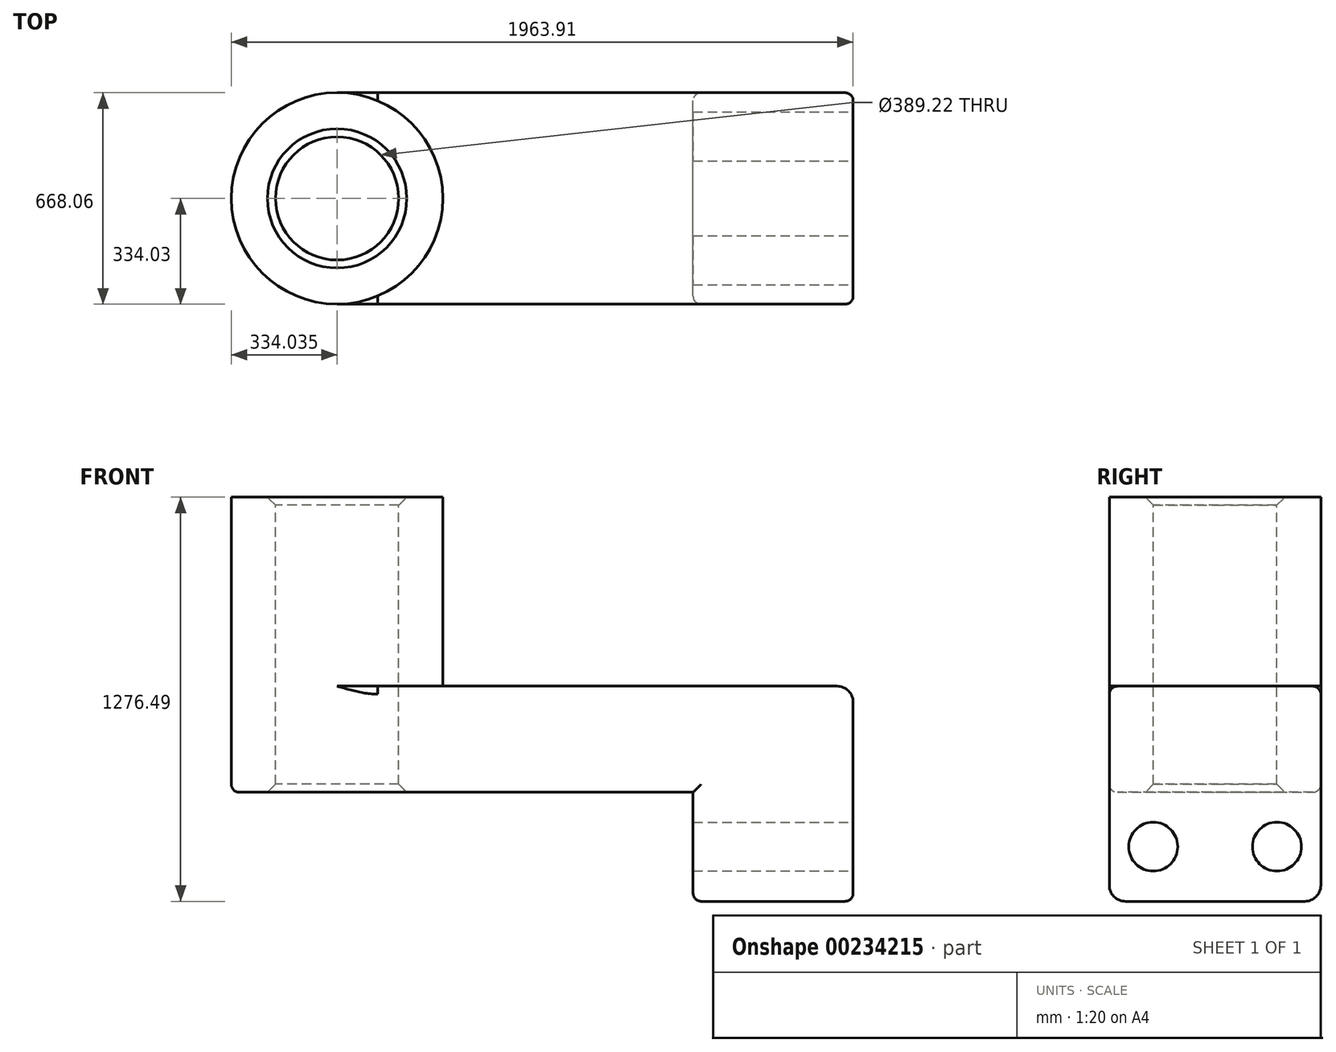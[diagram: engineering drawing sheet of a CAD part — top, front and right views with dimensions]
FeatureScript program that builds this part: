
annotation { "Feature Type Name" : "Feature", "Feature Type Description" : "" }
export const myFeature = defineFeature(function(context is Context, id is Id, definition is map)
    precondition{}
    {
        {
            var Q0;
            Q0=qCreatedBy(makeId("Top.planeOp"),FACE);
            var sketch = newSketch(context, id + "F0", { "sketchPlane" : qUnion([Q0])});
            skLineSegment(sketch, "E0.bottom", {"start": v(-814.94, 334.03) * mm, "end": v(814.94, 334.03) * mm});
            skLineSegment(sketch, "E0.top", {"start": v(-814.94, -334.03) * mm, "end": v(814.94, -334.03) * mm});
            skLineSegment(sketch, "E0.left", {"start": v(-814.94, 334.03) * mm, "end": v(-814.94, -334.03) * mm});
            skLineSegment(sketch, "E0.right", {"start": v(814.94, 334.03) * mm, "end": v(814.94, -334.03) * mm});
            skPoint(sketch, "E0.middle", {"position": v(0, 0) * mm});
            skCircle(sketch, "E1", {"center": v(-814.94, 0) * mm, "radius": 334.03 * mm});
            skCircle(sketch, "E2", {"center": v(-814.94, 0) * mm, "radius": 194.61 * mm});
            skSolve(sketch);
        }
        {
            var Q0;
            Q0 = qSketchRegion(id + "F0", true);
            extrude(context, id + "F1", {"entities" : qUnion([Q0]), "oppositeDirection" : true, "depth" : 335.28 * mm});
        }
        {
            var Q0;
            {var subQ1=sQuery(id+"F0.wireOp",EDGE,"E0.left");var subQ3=sQuery(id+"F0.wireOp",EDGE,"E2");var subQ4=makeQuery(id+"F0.imprint","INTERSECT",VERTEX,{"disambiguationData":[OD(0.0)],"derivedFrom":[subQ1,subQ3]});Q0=makeQuery(id+"F0.imprint","IMPRINT",FACE,{"disambiguationData":[TD([[makeQuery(id+"F0.imprint","IMPRINT",EDGE,{"disambiguationData":[TD([[subQ4,-1.0]])],"derivedFrom":subQ3}),-1.0]])]});}
            var Q1;
            {var subQ1=sQuery(id+"F0.wireOp",EDGE,"E0.left");var subQ3=sQuery(id+"F0.wireOp",EDGE,"E2");var subQ4=makeQuery(id+"F0.imprint","INTERSECT",VERTEX,{"disambiguationData":[OD(0.0)],"derivedFrom":[subQ1,subQ3]});Q1=makeQuery(id+"F0.imprint","IMPRINT",FACE,{"disambiguationData":[TD([[makeQuery(id+"F0.imprint","IMPRINT",EDGE,{"disambiguationData":[TD([[subQ4,1.0]])],"derivedFrom":subQ3}),-1.0]])]});}
            extrude(context, id + "F2", {"entities" : qUnion([Q0, Q1]), "operationType" : NewBodyOperationType.ADD, "depth" : 596.9 * mm});
        }
        {
            var Q0;
            Q0=makeQuery(id+"F1.opExtrude","SWEPT_FACE",FACE,{"disambiguationData":[OSD([sQuery(id+"F0.wireOp",EDGE,"E0.right")])]});
            var sketch = newSketch(context, id + "F3", { "sketchPlane" : qUnion([Q0])});
            skLineSegment(sketch, "E3.bottom", {"start": v(-334.03, 0) * mm, "end": v(334.03, 0) * mm});
            skLineSegment(sketch, "E3.top", {"start": v(-334.03, -679.59) * mm, "end": v(334.03, -679.59) * mm});
            skLineSegment(sketch, "E3.left", {"start": v(-334.03, 0) * mm, "end": v(-334.03, -679.59) * mm});
            skLineSegment(sketch, "E3.right", {"start": v(334.03, 0) * mm, "end": v(334.03, -679.59) * mm});
            skCircle(sketch, "E4", {"center": v(-195.4, -506.81) * mm, "radius": 77.27 * mm});
            skLineSegment(sketch, "E5", {"start": v(0, -335.28) * mm, "end": v(0, -679.59) * mm, "construction": true});
            skCircle(sketch, "E6.MirrorC", {"center": v(195.4, -506.81) * mm, "radius": 77.27 * mm});
            skSolve(sketch);
        }
        {
            var Q0;
            Q0 = qSketchRegion(id + "F3", true);
            extrude(context, id + "F4", {"entities" : qUnion([Q0]), "operationType" : NewBodyOperationType.ADD, "oppositeDirection" : true, "depth" : 505.46 * mm});
        }
        {
            var Q0;
            Q0=makeQuery(id+"F2.opExtrude","CAP_EDGE",EDGE,{"disambiguationData":[OSD([sQuery(id+"F0.wireOp",EDGE,"E1")])],"isStart":true});
            var Q1;
            Q1=makeQuery(id+"F1.opExtrude","CAP_EDGE",EDGE,{"disambiguationData":[OSD([sQuery(id+"F0.wireOp",EDGE,"E0.right")])],"isStart":true});
            var Q2;
            Q2=makeQuery(id+"F4.opExtrude","SWEPT_EDGE",EDGE,{"disambiguationData":[OSD([sQuery(id+"F3.wireOp",EDGE,"E3.top"),sQuery(id+"F3.wireOp",EDGE,"E3.left")])]});
            var Q3;
            Q3=makeQuery(id+"F4.opExtrude","SWEPT_EDGE",EDGE,{"disambiguationData":[OSD([sQuery(id+"F3.wireOp",EDGE,"E3.top"),sQuery(id+"F3.wireOp",EDGE,"E3.right")])]});
            fillet(context, id + "F5", {"entities" : qUnion([Q0, Q1, Q2, Q3]), "radius" : 50.8 * mm, "tangentPropagation" : true, "allowEdgeOverflow" : false});
        }
        {
            var Q0;
            Q0=makeQuery(id+"F1.opExtrude","CAP_EDGE",EDGE,{"disambiguationData":[OSD([sQuery(id+"F0.wireOp",EDGE,"E0.top")])],"isStart":false});
            var Q1;
            Q1=makeQuery(id+"F1.opExtrude","CAP_EDGE",EDGE,{"disambiguationData":[OSD([sQuery(id+"F0.wireOp",EDGE,"E1")])],"isStart":false});
            var Q2;
            Q2=makeQuery(id+"F1.opExtrude","CAP_EDGE",EDGE,{"disambiguationData":[OSD([sQuery(id+"F0.wireOp",EDGE,"E0.bottom")])],"isStart":false});
            var Q3;
            Q3=makeQuery(id+"F4.opExtrude","CAP_EDGE",EDGE,{"disambiguationData":[OSD([sQuery(id+"F3.wireOp",EDGE,"E3.right")])],"isStart":false});
            var Q4;
            Q4=makeQuery(id+"F4.opExtrude","CAP_EDGE",EDGE,{"disambiguationData":[OSD([sQuery(id+"F3.wireOp",EDGE,"E3.left")])],"isStart":false});
            var Q5;
            Q5=makeQuery(id+"F1.opExtrude","CAP_EDGE",EDGE,{"disambiguationData":[OSD([sQuery(id+"F0.wireOp",EDGE,"E0.bottom")])],"isStart":true});
            var Q6;
            Q6=makeQuery(id+"F1.opExtrude","CAP_EDGE",EDGE,{"disambiguationData":[OSD([sQuery(id+"F0.wireOp",EDGE,"E0.top")])],"isStart":true});
            fillet(context, id + "F6", {"entities" : qUnion([Q0, Q1, Q2, Q3, Q4, Q5, Q6]), "radius" : 25.4 * mm, "tangentPropagation" : true, "allowEdgeOverflow" : false});
        }
        {
            var Q0;
            Q0=makeQuery(id+"F2.opExtrude","CAP_EDGE",EDGE,{"disambiguationData":[OSD([sQuery(id+"F0.wireOp",EDGE,"E2")])],"isStart":false});
            var Q1;
            Q1=makeQuery(id+"F1.opExtrude","CAP_EDGE",EDGE,{"disambiguationData":[OSD([sQuery(id+"F0.wireOp",EDGE,"E2")])],"isStart":false});
            chamfer(context, id + "F7", {"entities" : qUnion([Q0, Q1]), "width" : 25.4 * mm, "tangentPropagation" : true});
        }
    });
